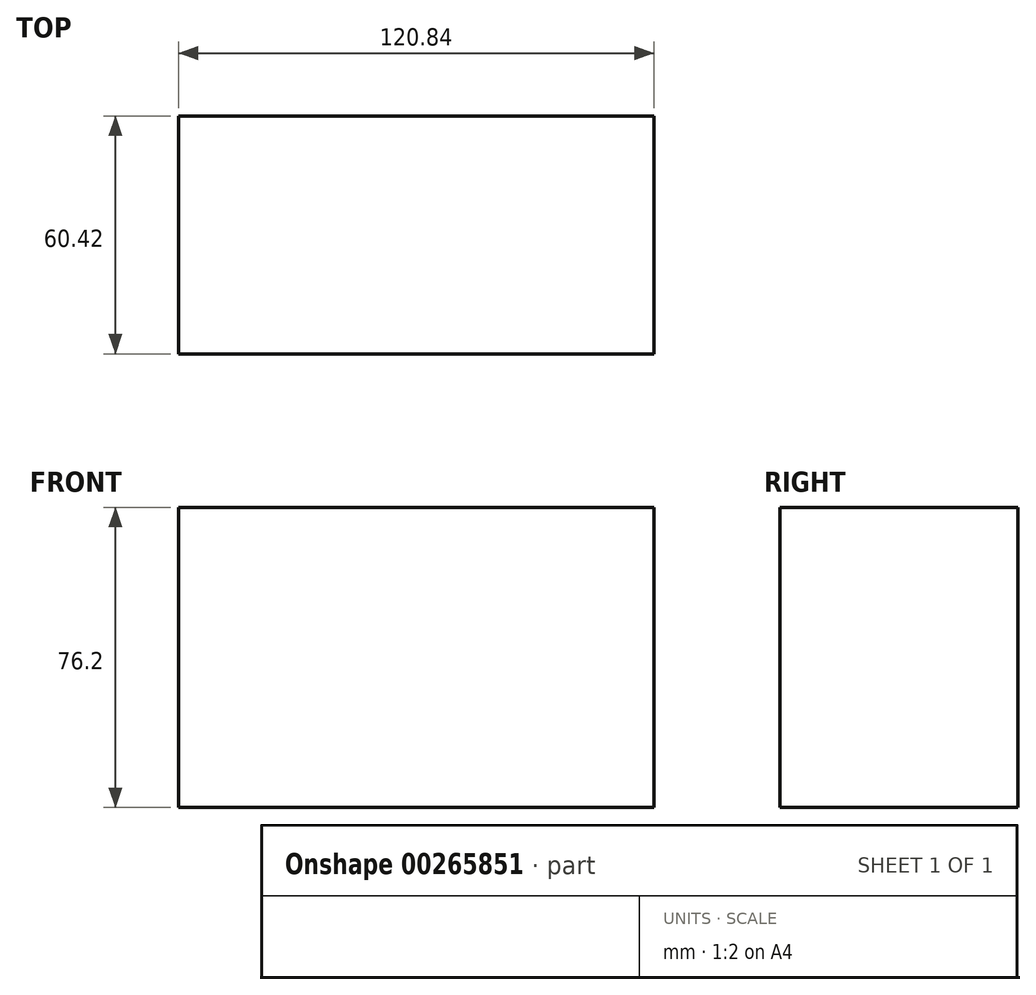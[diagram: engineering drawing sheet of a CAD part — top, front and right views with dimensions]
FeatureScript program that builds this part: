
annotation { "Feature Type Name" : "Feature", "Feature Type Description" : "" }
export const myFeature = defineFeature(function(context is Context, id is Id, definition is map)
    precondition{}
    {
        {
            var Q0;
            Q0=qCreatedBy(makeId("Top.planeOp"),FACE);
            var sketch = newSketch(context, id + "F0", { "sketchPlane" : qUnion([Q0])});
            skLineSegment(sketch, "E0.bottom", {"start": v(-60.42, 30.21) * mm, "end": v(60.42, 30.21) * mm});
            skLineSegment(sketch, "E0.top", {"start": v(-60.42, -30.21) * mm, "end": v(60.42, -30.21) * mm});
            skLineSegment(sketch, "E0.left", {"start": v(-60.42, 30.21) * mm, "end": v(-60.42, -30.21) * mm});
            skLineSegment(sketch, "E0.right", {"start": v(60.42, 30.21) * mm, "end": v(60.42, -30.21) * mm});
            skPoint(sketch, "E0.middle", {"position": v(0, 0) * mm});
            skSolve(sketch);
        }
        {
            var Q0;
            Q0 = qSketchRegion(id + "F0", true);
            extrude(context, id + "F1", {"entities" : qUnion([Q0]), "depth" : 76.2 * mm});
        }
    });
